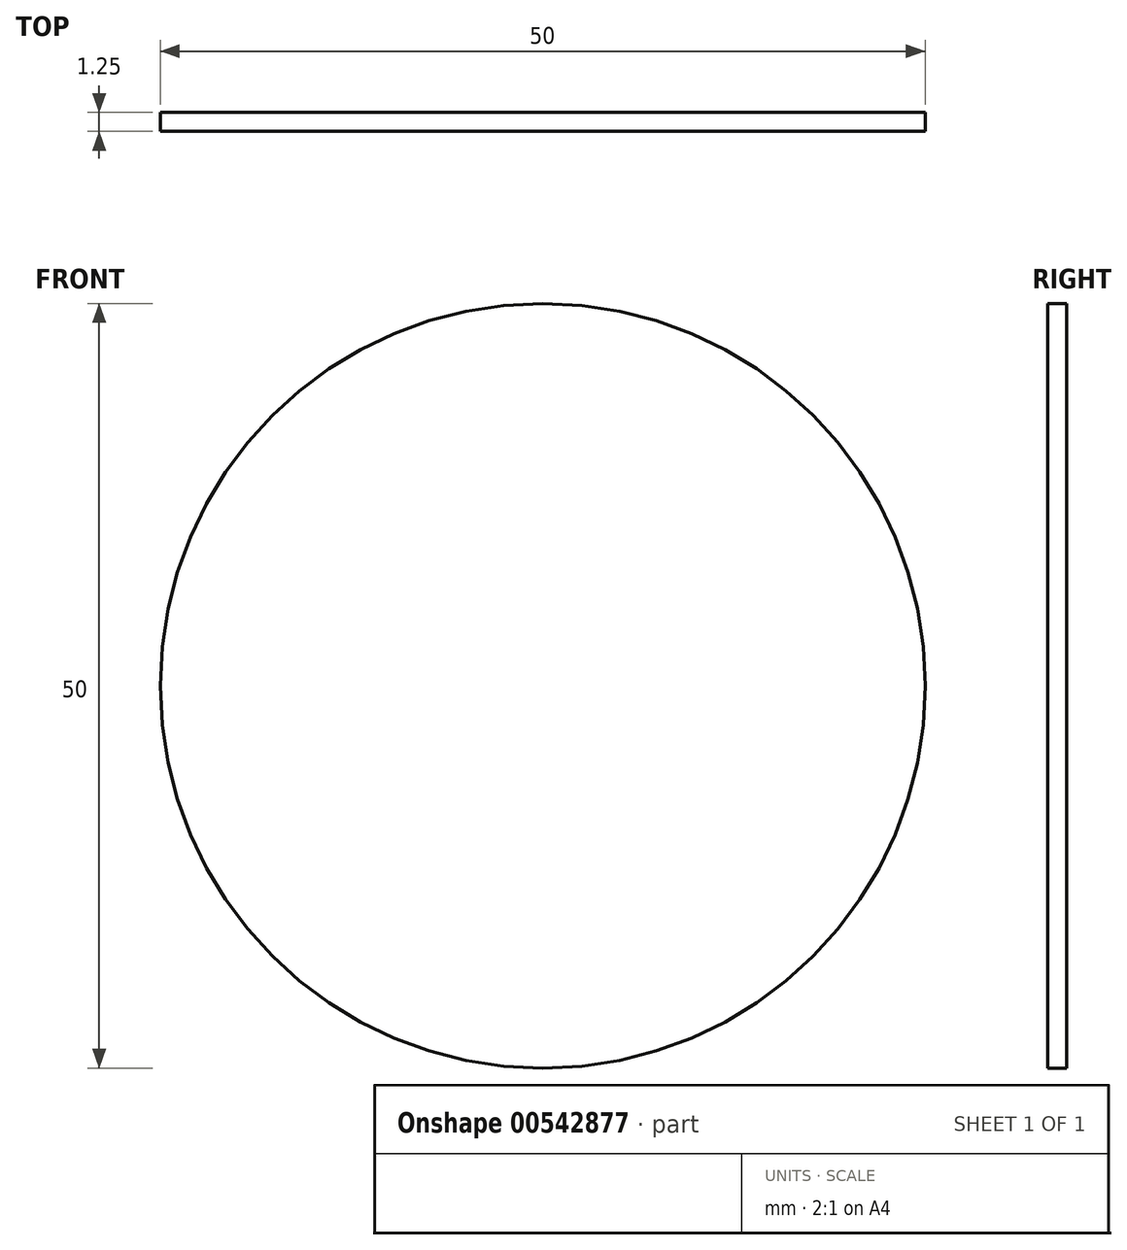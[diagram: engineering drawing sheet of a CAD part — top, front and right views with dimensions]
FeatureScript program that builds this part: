
annotation { "Feature Type Name" : "Feature", "Feature Type Description" : "" }
export const myFeature = defineFeature(function(context is Context, id is Id, definition is map)
    precondition{}
    {
        {
            var Q0;
            Q0=qCreatedBy(makeId("Front.planeOp"),FACE);
            var sketch = newSketch(context, id + "F0", { "sketchPlane" : qUnion([Q0])});
            skCircle(sketch, "E0", {"center": v(0, 0) * mm, "radius": 25 * mm});
            skSolve(sketch);
        }
        {
            var Q0;
            Q0=makeQuery(id+"F0.imprint","IMPRINT",FACE,{"disambiguationData":[TD([[makeQuery(id+"F0.imprint","IMPRINT",EDGE,{"derivedFrom":sQuery(id+"F0.wireOp",EDGE,"E0")}),1.0]])]});
            extrude(context, id + "F1", {"entities" : qUnion([Q0]), "depth" : 1.25 * mm, "offsetDistance" : 25 * mm});
        }
    });
